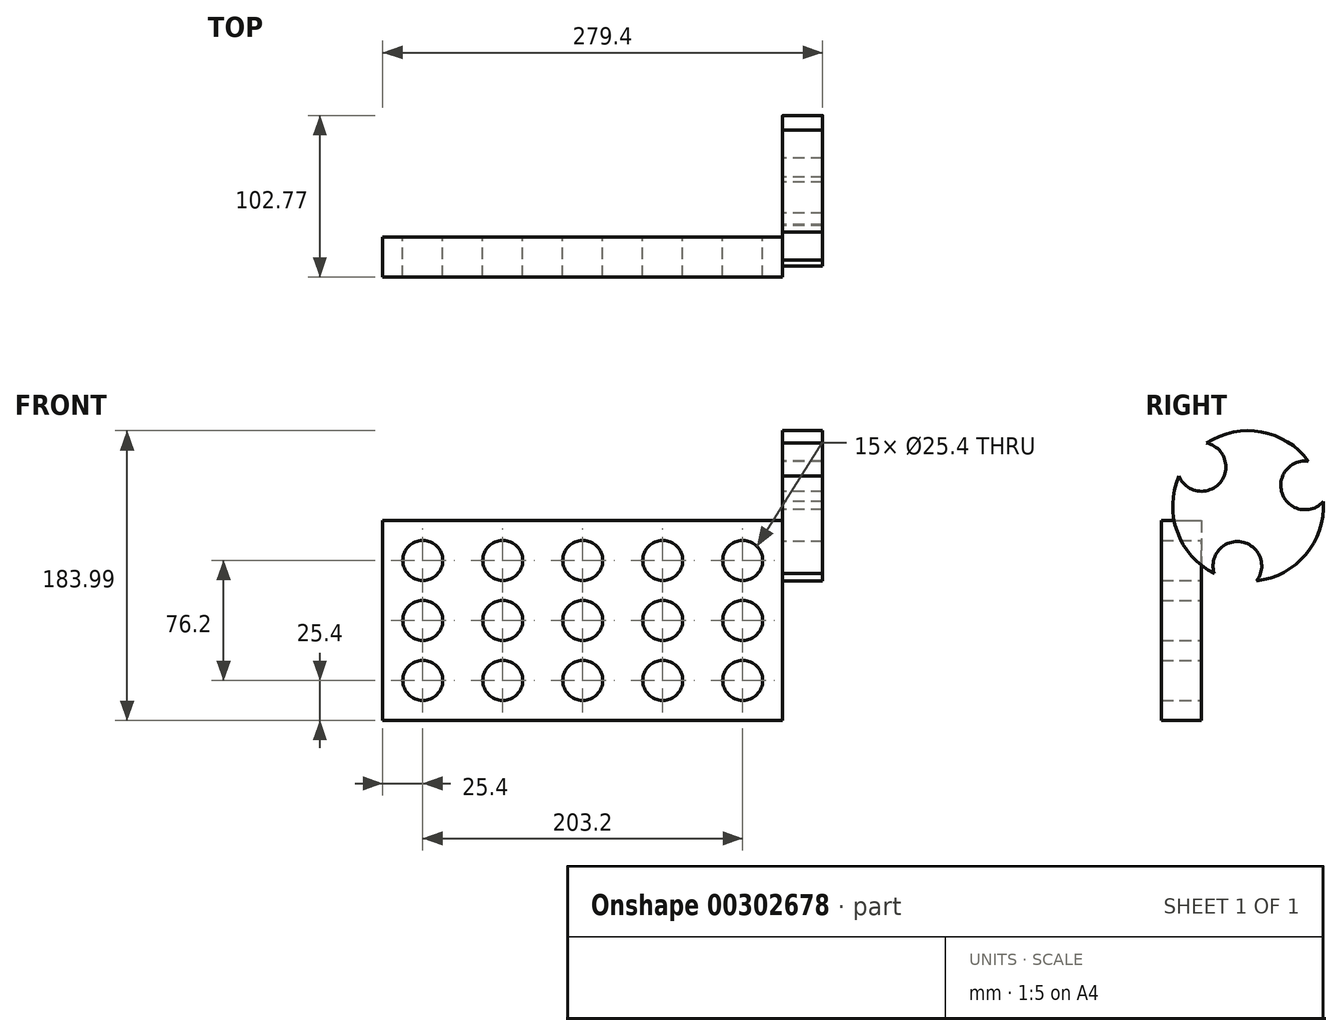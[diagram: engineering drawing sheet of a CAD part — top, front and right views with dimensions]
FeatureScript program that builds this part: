
annotation { "Feature Type Name" : "Feature", "Feature Type Description" : "" }
export const myFeature = defineFeature(function(context is Context, id is Id, definition is map)
    precondition{}
    {
        {
            var Q0;
            Q0=qCreatedBy(makeId("Front.planeOp"),FACE);
            var sketch = newSketch(context, id + "F0", { "sketchPlane" : qUnion([Q0])});
            skLineSegment(sketch, "E0.bottom", {"start": v(0, 0) * mm, "end": v(-254, 0) * mm});
            skLineSegment(sketch, "E0.top", {"start": v(0, -127) * mm, "end": v(-254, -127) * mm});
            skLineSegment(sketch, "E0.left", {"start": v(0, 0) * mm, "end": v(0, -127) * mm});
            skLineSegment(sketch, "E0.right", {"start": v(-254, 0) * mm, "end": v(-254, -127) * mm});
            skCircle(sketch, "E1", {"center": v(-228.6, -25.4) * mm, "radius": 12.7 * mm});
            skCircle(sketch, "E2.0.1.0", {"center": v(-228.6, -63.5) * mm, "radius": 12.7 * mm});
            skCircle(sketch, "E2.0.2.0", {"center": v(-228.6, -101.6) * mm, "radius": 12.7 * mm});
            skCircle(sketch, "E2.1.0.0", {"center": v(-177.8, -25.4) * mm, "radius": 12.7 * mm});
            skCircle(sketch, "E2.1.1.0", {"center": v(-177.8, -63.5) * mm, "radius": 12.7 * mm});
            skCircle(sketch, "E2.1.2.0", {"center": v(-177.8, -101.6) * mm, "radius": 12.7 * mm});
            skCircle(sketch, "E2.2.0.0", {"center": v(-127, -25.4) * mm, "radius": 12.7 * mm});
            skCircle(sketch, "E2.2.1.0", {"center": v(-127, -63.5) * mm, "radius": 12.7 * mm});
            skCircle(sketch, "E2.2.2.0", {"center": v(-127, -101.6) * mm, "radius": 12.7 * mm});
            skCircle(sketch, "E2.3.0.0", {"center": v(-76.2, -25.4) * mm, "radius": 12.7 * mm});
            skCircle(sketch, "E2.3.1.0", {"center": v(-76.2, -63.5) * mm, "radius": 12.7 * mm});
            skCircle(sketch, "E2.3.2.0", {"center": v(-76.2, -101.6) * mm, "radius": 12.7 * mm});
            skCircle(sketch, "E2.4.0.0", {"center": v(-25.4, -25.4) * mm, "radius": 12.7 * mm});
            skCircle(sketch, "E2.4.1.0", {"center": v(-25.4, -63.5) * mm, "radius": 12.7 * mm});
            skCircle(sketch, "E2.4.2.0", {"center": v(-25.4, -101.6) * mm, "radius": 12.7 * mm});
            skLineSegment(sketch, "E2.direction1", {"start": v(-228.6, -25.4) * mm, "end": v(-177.8, -25.4) * mm, "construction": true});
            skLineSegment(sketch, "E2.direction2", {"start": v(-228.6, -25.4) * mm, "end": v(-228.6, -63.5) * mm, "construction": true});
            skSolve(sketch);
        }
        {
            var Q0;
            Q0 = qSketchRegion(id + "F0", true);
            extrude(context, id + "F1", {"entities" : qUnion([Q0]), "depth" : 25.4 * mm});
        }
        {
            var Q0;
            Q0=qCreatedBy(makeId("Right.planeOp"),FACE);
            var sketch = newSketch(context, id + "F2", { "sketchPlane" : qUnion([Q0])});
            skArc(sketch, "E3", {"start": v(-14.36, 28.24) * mm, "mid": v(11.83, 24.03) * mm, "end": v(3.22, 49.12) * mm});
            skArc(sketch, "E4", {"start": v(-14.36, 28.24) * mm, "mid": v(66.13, -21.67) * mm, "end": v(3.22, 49.12) * mm});
            skArc(sketch, "E5.1.0", {"start": v(34.92, -38.4) * mm, "mid": v(25.47, -13.62) * mm, "end": v(8.05, -33.62) * mm});
            skArc(sketch, "E5.2.0", {"start": v(68, 37.6) * mm, "mid": v(51.26, 17.02) * mm, "end": v(77.3, 11.93) * mm});
            skSolve(sketch);
        }
        {
            var Q0;
            {var subQ3=sQuery(id+"F2.wireOp",EDGE,"E3");Q0=makeQuery(id+"F2.imprint","IMPRINT",FACE,{"disambiguationData":[TD([[makeQuery(id+"F2.imprint","IMPRINT",EDGE,{"derivedFrom":subQ3}),-1.0]])]});}
            extrude(context, id + "F3", {"entities" : qUnion([Q0]), "operationType" : NewBodyOperationType.ADD, "depth" : 25.4 * mm});
        }
    });
